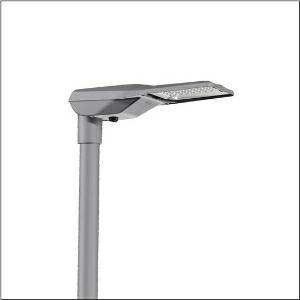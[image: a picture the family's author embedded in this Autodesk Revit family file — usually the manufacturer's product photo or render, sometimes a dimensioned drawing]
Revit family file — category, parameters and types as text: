
# Revit family: streetlight_sl_21_iq_mini___p0_5a_5xe2v31u08jb_c08b
name_source: partatom
category: Lighting Fixtures
units: mm (PartAtom-declared; Revit-internal decimal feet)

## family parameters
Cut with Voids When Loaded = No
Host = Face
Light Source = No
Part Type = Normal
Room Calculation Point = No
Round Connector Dimension = Use Diameter
Shared = No

## types (1)
- --- (1 x LED, 11020 lm, 72.5 W, 3000K)
    Apparent Load = 73 VA
    CIE Flux Codes = 37 73 96 100 100
    Color Rendering = 70
    Color Temperature = 3000K
    Default Elevation = 1800 mm
    Description = Streetlight SL 21 iQ mini, mast luminaire, primary light control with lens, of PMMA, primary optical cover: cover, of toughened safety glass, transparent, light distribution: P0.5a, light emission: direct distribution, primary light characteristic: asymmetric, installation type: post-top, side-entry, LED, High Power LED, rated luminous flux: 11.020lm, luminous efficacy: 152lm/W, light colour: 730, colour temperature: 3000K, control gear: iQ-Street Remote, D4i with power reduction, control: pre-setting: logarithmic dimming characteristic, Street-Remote, Auto-Match, Temp-Guard, Lumen-Switch, Night-Set, Smart-Wire, Light-Fading, Desk-Remote (wireless, voltage-free reading and setting of iQ features in the workshop via application-optimized NFC function/RFID function), optimised constant luminous flux control (CLO 2.0), mains connection: 220..240V, AC, 50/60Hz, start of lifetime: 73W, end of service life: 76W, reduction: 33W, luminaire housing, of diecast aluminium, powder-coated, SITECO metallic grey (DB 702S), corrosivity category C5 high according to DIN EN ISO 12944, please order mast flange separately, inclination adjustable: 0°, 5°, 10°, 15°, sealing non-destructively replaceable, multi-level sealing system, length: 628mm, width: 235mm, height: 110mm, mast flange for spigot size: 42mm (side-entry): 5XC10008XM4, 60/48mm (side-entry/post-top): 5XC10108XM2, 76/60mm (side-entry/post-top): 5XC10108XM1, mounting height: 4..8m, Smart Interface below, protection rating (complete): IP66, insulation class (complete): insulation class II (safety insulation), certification: CE, ENEC, ENEC+, VDE, impact resistance: IK10, permissible operating ambient temperature for outdoor applications: -40..+50°C, standard-compliant lighting for roads and squares, packaging unit: 1 piece

Light Distribution: P0.5a
    Height = 110 mm
    Lamp = 1 x LED
    Lamp Light Flux = 11020 lm
    Lamp Power = 72.5 W
    Lamp count = 1
    Length = 625 mm
    Luminous efficacy = 152 lm/W
    Manufacturer = Siteco
    ModVariant = No
    Model = 5XE2V31U08JB
    Number of Poles = 1
    OnlyDefault = Yes
    Power Factor = 1
    Product Name = Streetlight SL 21 iQ mini | P0.5a
    Product group = mast luminaire | pylon top
    ProductGroupID = 6100
    Protection Class = Protection class II
    Protection Degree = IP 66
    RLX_Detail_Level = 1
    RLX_Emergency_Light_Flux = 0 lm
    RLX_Emergency_Type = 0
    RLX_Emergency_Type_DB = No
    RlxData = <blob elided: 92245 chars, md5=fd674a38>
    Socket = socket
    Standby Power = 0 W
    System Light Flux = 11020 lm
    System Power = 73 W
    Type Comments = factory setting: luminous flux: 100 % | dim-lin: 254 | 755 mA
    Type Image = l_1003516.jpg
    URL = http://relux.com
    VarID = @adj_077205
    Voltage = 0 V
    Weight = 0.00 kg
    Width = 234 mm

## geometry (parser evidence)
native form markers: Blend x4, Sweep x9
no freeform markers — native parametric forms only
